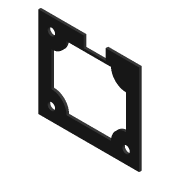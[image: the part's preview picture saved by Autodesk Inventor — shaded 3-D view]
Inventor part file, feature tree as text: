
AUTODESK INVENTOR PART (.ipt)
format: ipt  version: 2015 SP1 (Build 190203100, 203)  size: 146,432 bytes
history: native  units: mm
features: extrude x2, other x1, sketch x1
ambient origin geometry x8: Origin, YZ Plane, XZ Plane, XY Plane, X Axis, Y Axis, Z Axis, Center Point
bodies: Body1 (feature_tree)
feature tree (4):
  other  "Твердое тело1"
  sketch  "Эскиз1"
  extrude  "Выдавливание1"  Depth=1.0mm TaperAngle=0.0deg
  extrude  "Выдавливание2"  Depth=10.0mm TaperAngle=0.0deg
